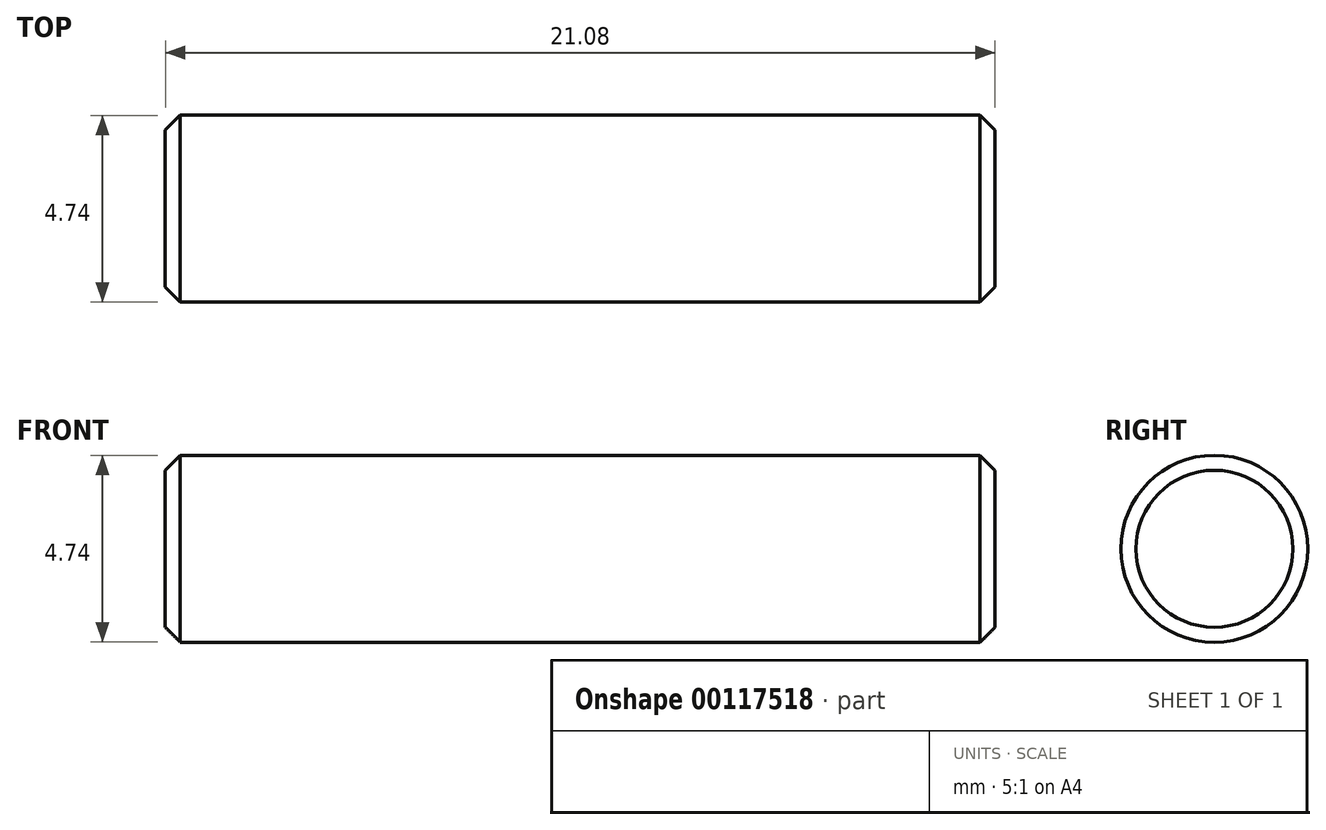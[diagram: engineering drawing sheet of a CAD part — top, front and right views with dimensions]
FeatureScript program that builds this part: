
annotation { "Feature Type Name" : "Feature", "Feature Type Description" : "" }
export const myFeature = defineFeature(function(context is Context, id is Id, definition is map)
    precondition{}
    {
        {
            var Q0;
            Q0=qCreatedBy(makeId("Right.planeOp"),FACE);
            var sketch = newSketch(context, id + "F0", { "sketchPlane" : qUnion([Q0])});
            skCircle(sketch, "E0", {"center": v(0, 0) * mm, "radius": 2.37 * mm});
            skSolve(sketch);
        }
        {
            var Q0;
            Q0 = qSketchRegion(id + "F0", true);
            extrude(context, id + "F1", {"entities" : qUnion([Q0]), "depth" : 21.08 * mm, "symmetric" : true});
        }
        {
            var Q0;
            Q0=makeQuery(id+"F1.opExtrude","CAP_EDGE",EDGE,{"disambiguationData":[OSD([sQuery(id+"F0.wireOp",EDGE,"E0")])],"isStart":false});
            var Q1;
            Q1=makeQuery(id+"F1.opExtrude","CAP_EDGE",EDGE,{"disambiguationData":[OSD([sQuery(id+"F0.wireOp",EDGE,"E0")])],"isStart":true});
            chamfer(context, id + "F2", {"entities" : qUnion([Q0, Q1]), "width" : 0.38 * mm, "tangentPropagation" : true});
        }
    });
